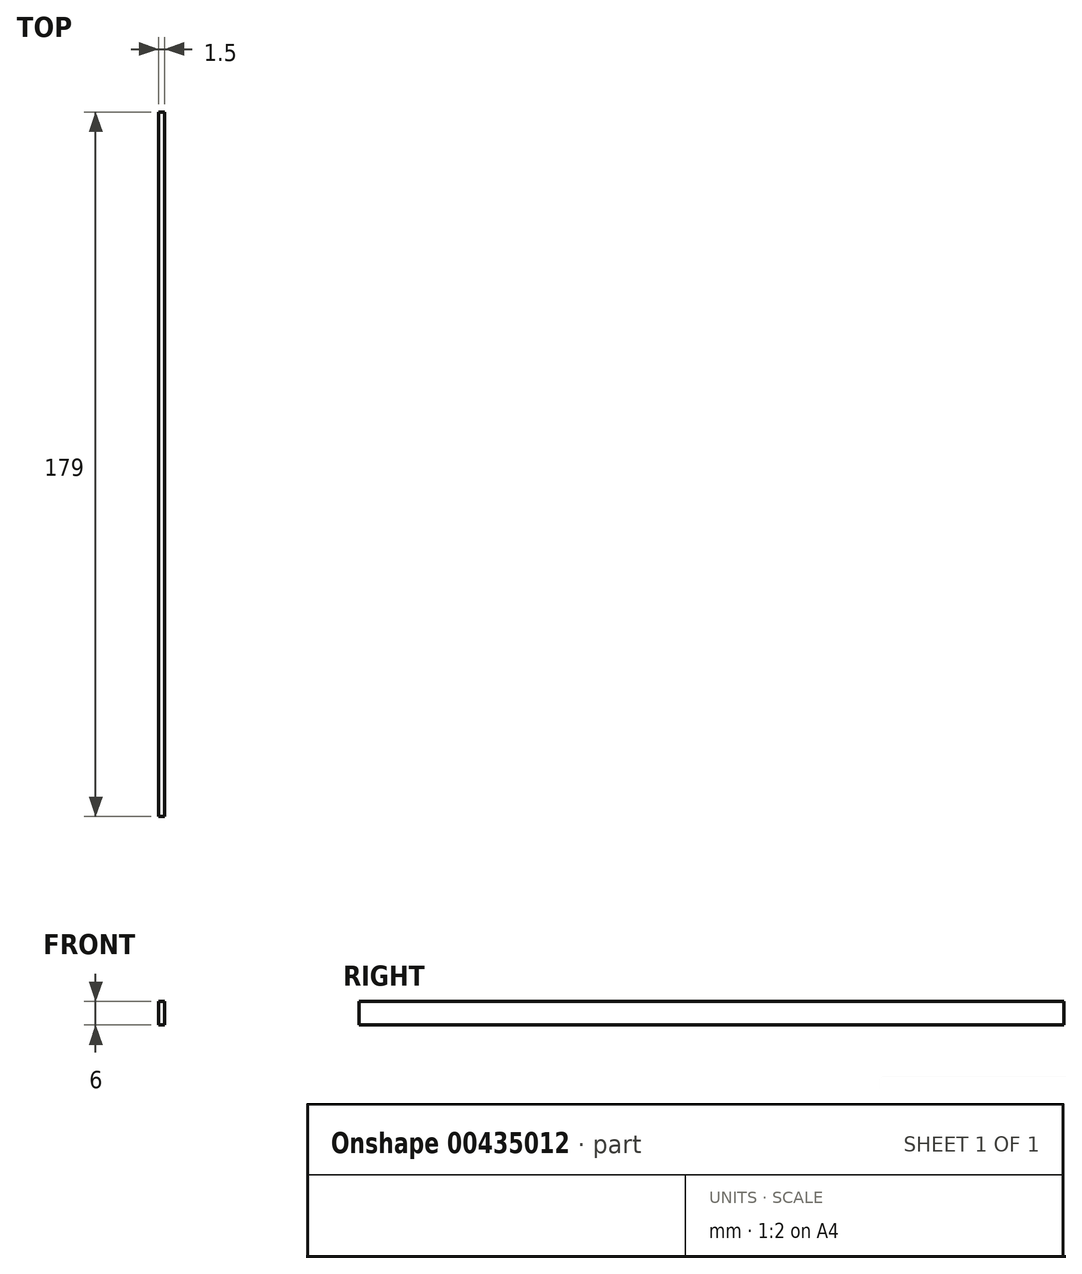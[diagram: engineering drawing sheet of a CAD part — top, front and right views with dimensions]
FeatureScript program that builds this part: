
annotation { "Feature Type Name" : "Feature", "Feature Type Description" : "" }
export const myFeature = defineFeature(function(context is Context, id is Id, definition is map)
    precondition{}
    {
        {
            var Q0;
            Q0=qCreatedBy(makeId("Right.planeOp"),FACE);
            var sketch = newSketch(context, id + "F0", { "sketchPlane" : qUnion([Q0])});
            skLineSegment(sketch, "E0.bottom", {"start": v(0, 0) * mm, "end": v(179, 0) * mm});
            skLineSegment(sketch, "E0.top", {"start": v(0, 6) * mm, "end": v(179, 6) * mm});
            skLineSegment(sketch, "E0.left", {"start": v(0, 0) * mm, "end": v(0, 6) * mm});
            skLineSegment(sketch, "E0.right", {"start": v(179, 0) * mm, "end": v(179, 6) * mm});
            skSolve(sketch);
        }
        {
            var Q0;
            Q0 = qSketchRegion(id + "F0", true);
            extrude(context, id + "F1", {"entities" : qUnion([Q0]), "depth" : 1.5 * mm});
        }
    });
